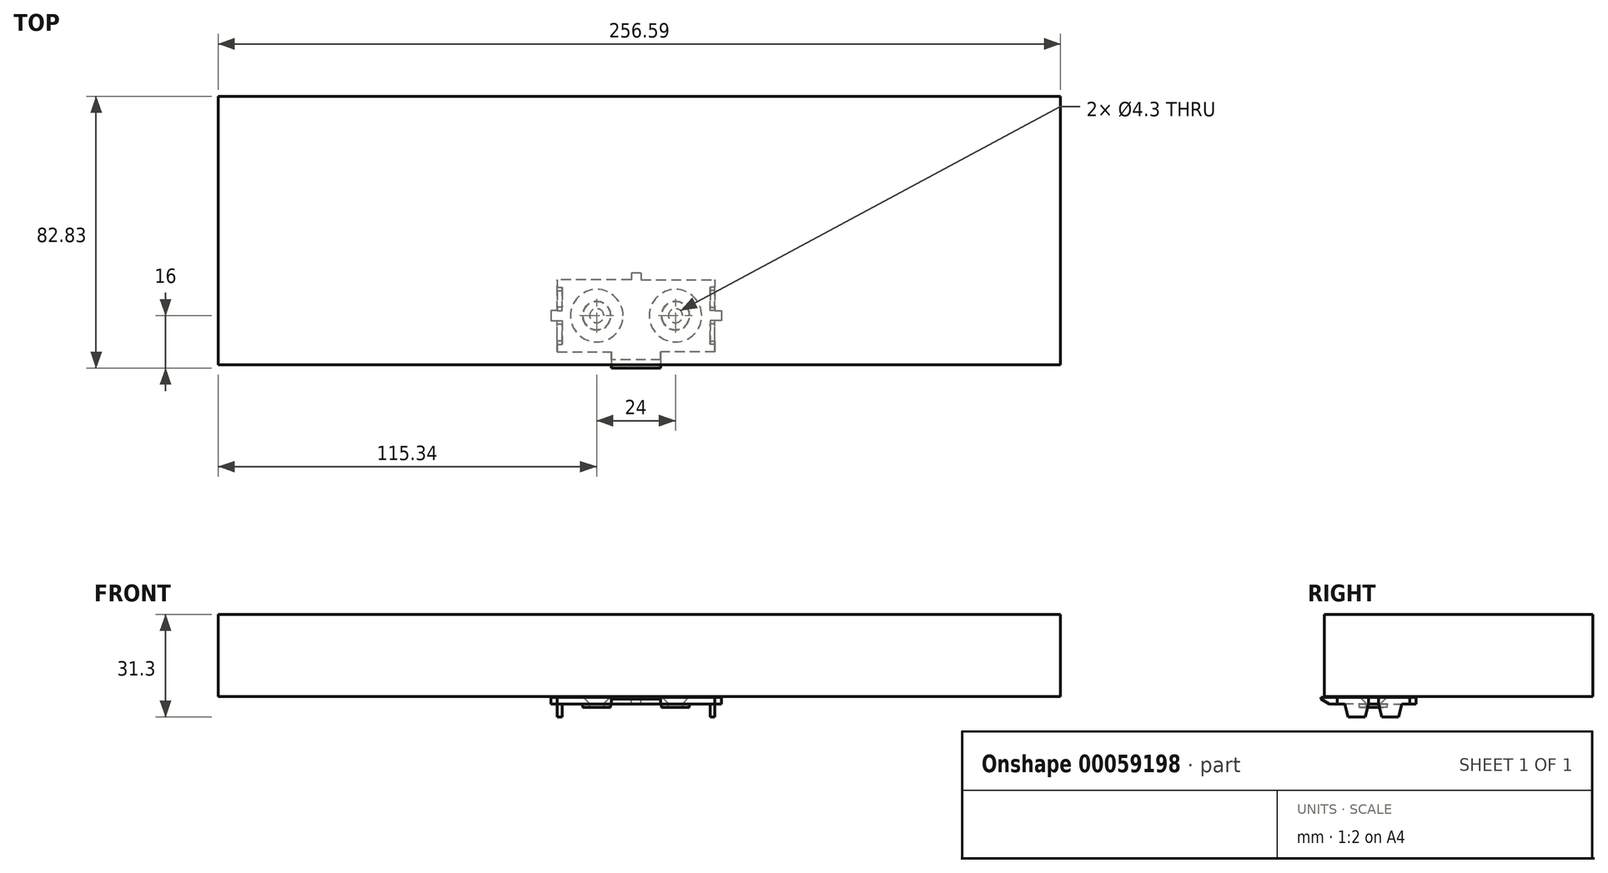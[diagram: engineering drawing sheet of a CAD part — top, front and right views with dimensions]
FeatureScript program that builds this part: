
annotation { "Feature Type Name" : "Feature", "Feature Type Description" : "" }
export const myFeature = defineFeature(function(context is Context, id is Id, definition is map)
    precondition{}
    {
        {
            assignVariable(context, id + "F0", {"name" : "lidLength", "anyValue" : 48 * mm});
        }
        {
            assignVariable(context, id + "F1", {"name" : "lidWidth", "anyValue" : 22 * mm});
        }
        {
            assignVariable(context, id + "F2", {"name" : "lidThickness", "anyValue" : 2 * mm});
        }
        {
            assignVariable(context, id + "F3", {"name" : "lidSnapDistFromTop", "anyValue" : 6 * mm});
        }
        {
            var Q0;
            Q0=qCreatedBy(makeId("Top.planeOp"),FACE);
            cPlane(context, id + "F4", {"entities" : qUnion([Q0]), "cplaneType" : CPlaneType.OFFSET, "offset" : 0.3 * mm, "width" : 150 * mm, "height" : 150 * mm});
        }
        {
            var Q0;
            Q0=qCreatedBy(makeId("Top.planeOp"),FACE);
            cPlane(context, id + "F5", {"entities" : qUnion([Q0]), "cplaneType" : CPlaneType.OFFSET, "offset" : getVariable(context, 'lidThickness'), "oppositeDirection" : true, "width" : 150 * mm, "height" : 150 * mm});
        }
        {
            var Q0;
            Q0=qCreatedBy(makeId("Top.planeOp"),FACE);
            cPlane(context, id + "F6", {"entities" : qUnion([Q0]), "cplaneType" : CPlaneType.OFFSET, "offset" : getVariable(context, 'lidSnapDistFromTop'), "oppositeDirection" : true, "width" : 150 * mm, "height" : 150 * mm});
        }
        {
            var Q0;
            Q0=qCreatedBy(makeId("Top.planeOp"),FACE);
            cPlane(context, id + "F7", {"entities" : qUnion([Q0]), "cplaneType" : CPlaneType.OFFSET, "offset" : 3 * mm, "oppositeDirection" : true, "width" : 150 * mm, "height" : 150 * mm});
        }
        {
            var Q0;
            Q0=qCreatedBy(makeId("Right.planeOp"),FACE);
            cPlane(context, id + "F8", {"entities" : qUnion([Q0]), "cplaneType" : CPlaneType.OFFSET, "offset" : getVariable(context, 'lidLength') / 2, "oppositeDirection" : true, "width" : 150 * mm, "height" : 150 * mm});
        }
        {
            var Q0;
            Q0=qCreatedBy(makeId("Front.planeOp"),FACE);
            cPlane(context, id + "F9", {"entities" : qUnion([Q0]), "cplaneType" : CPlaneType.OFFSET, "offset" : getVariable(context, 'lidWidth'), "oppositeDirection" : true, "width" : 150 * mm, "height" : 150 * mm});
        }
        {
            var Q0;
            Q0=qCreatedBy(makeId("Top.planeOp"),FACE);
            var sketch = newSketch(context, id + "F10", { "sketchPlane" : qUnion([Q0])});
            skLineSegment(sketch, "E0", {"start": v(-7.5, 0) * mm, "end": v(-24, 0) * mm});
            skLineSegment(sketch, "E1", {"start": v(-24, 0) * mm, "end": v(-24, 9.5) * mm});
            skLineSegment(sketch, "E2", {"start": v(-24, 9.5) * mm, "end": v(-26, 9.5) * mm});
            skLineSegment(sketch, "E3", {"start": v(-26, 9.5) * mm, "end": v(-26, 12.5) * mm});
            skLineSegment(sketch, "E4", {"start": v(-26, 12.5) * mm, "end": v(-24, 12.5) * mm});
            skLineSegment(sketch, "E5", {"start": v(-24, 12.5) * mm, "end": v(-24, 22) * mm});
            skLineSegment(sketch, "E6", {"start": v(-24, 22) * mm, "end": v(-1.5, 22) * mm});
            skLineSegment(sketch, "E7", {"start": v(-1.5, 22) * mm, "end": v(-1.5, 24) * mm});
            skLineSegment(sketch, "E8", {"start": v(-1.5, 24) * mm, "end": v(0, 24) * mm});
            skLineSegment(sketch, "E9", {"start": v(-7.5, 0) * mm, "end": v(-7.5, -5) * mm});
            skLineSegment(sketch, "E10", {"start": v(-7.5, -5) * mm, "end": v(0, -5) * mm});
            skLineSegment(sketch, "E11.MirrorCS", {"start": v(24, 9.5) * mm, "end": v(26, 9.5) * mm, "construction": true});
            skLineSegment(sketch, "E12.MirrorCS", {"start": v(7.5, 0) * mm, "end": v(7.5, -5) * mm, "construction": true});
            skLineSegment(sketch, "E13.MirrorCS", {"start": v(26, 12.5) * mm, "end": v(24, 12.5) * mm, "construction": true});
            skLineSegment(sketch, "E14.MirrorCS", {"start": v(1.5, 24) * mm, "end": v(0, 24) * mm, "construction": true});
            skLineSegment(sketch, "E15.MirrorCS", {"start": v(26, 9.5) * mm, "end": v(26, 12.5) * mm, "construction": true});
            skLineSegment(sketch, "E16.MirrorCS", {"start": v(1.5, 22) * mm, "end": v(1.5, 24) * mm, "construction": true});
            skLineSegment(sketch, "E17.MirrorCS", {"start": v(7.5, 0) * mm, "end": v(24, 0) * mm, "construction": true});
            skLineSegment(sketch, "E18.MirrorCS", {"start": v(24, 0) * mm, "end": v(24, 9.5) * mm, "construction": true});
            skLineSegment(sketch, "E19.MirrorCS", {"start": v(7.5, -5) * mm, "end": v(0, -5) * mm, "construction": true});
            skLineSegment(sketch, "E20.MirrorCS", {"start": v(24, 22) * mm, "end": v(1.5, 22) * mm, "construction": true});
            skLineSegment(sketch, "E21.MirrorCS", {"start": v(24, 12.5) * mm, "end": v(24, 22) * mm, "construction": true});
            skLineSegment(sketch, "E22", {"start": v(0, 24) * mm, "end": v(0, -5) * mm});
            skSolve(sketch);
        }
        {
            var Q0;
            Q0 = qSketchRegion(id + "F10", true);
            var Q1;
            Q1=qCreatedBy(id+"F5.planeOp",FACE);
            extrude(context, id + "F11", {"entities" : qUnion([Q0]), "endBound" : BoundingType.UP_TO_SURFACE, "oppositeDirection" : true, "endBoundEntityFace" : qUnion([Q1]), "depth" : 25 * mm});
        }
        {
            var Q0;
            Q0=qCreatedBy(makeId("Top.planeOp"),FACE);
            var sketch = newSketch(context, id + "F12", { "sketchPlane" : qUnion([Q0])});
            skLineSegment(sketch, "E23.bottom", {"start": v(-24, 9.5) * mm, "end": v(-22.5, 9.5) * mm});
            skLineSegment(sketch, "E23.top", {"start": v(-24, 2.3) * mm, "end": v(-22.5, 2.3) * mm});
            skLineSegment(sketch, "E23.left", {"start": v(-24, 9.5) * mm, "end": v(-24, 2.3) * mm});
            skLineSegment(sketch, "E23.right", {"start": v(-22.5, 9.5) * mm, "end": v(-22.5, 2.3) * mm});
            skLineSegment(sketch, "E24.bottom", {"start": v(-24, 12.5) * mm, "end": v(-22.5, 12.5) * mm});
            skLineSegment(sketch, "E24.top", {"start": v(-24, 19.7) * mm, "end": v(-22.5, 19.7) * mm});
            skLineSegment(sketch, "E24.left", {"start": v(-24, 12.5) * mm, "end": v(-24, 19.7) * mm});
            skLineSegment(sketch, "E24.right", {"start": v(-22.5, 12.5) * mm, "end": v(-22.5, 19.7) * mm});
            skSolve(sketch);
        }
        {
            var Q0;
            Q0 = qSketchRegion(id + "F12", true);
            var Q1;
            Q1=qCreatedBy(id+"F6.planeOp",FACE);
            extrude(context, id + "F13", {"entities" : qUnion([Q0]), "operationType" : NewBodyOperationType.ADD, "endBound" : BoundingType.UP_TO_SURFACE, "oppositeDirection" : true, "endBoundEntityFace" : qUnion([Q1]), "depth" : 25 * mm});
        }
        {
            var Q0;
            Q0=qCreatedBy(makeId("Top.planeOp"),FACE);
            var sketch = newSketch(context, id + "F14", { "sketchPlane" : qUnion([Q0])});
            skCircle(sketch, "E25", {"center": v(-12, 11) * mm, "radius": 4.25 * mm});
            skSolve(sketch);
        }
        {
            var Q0;
            Q0 = qSketchRegion(id + "F14", true);
            var Q1;
            Q1=qCreatedBy(id+"F7.planeOp",FACE);
            extrude(context, id + "F15", {"entities" : qUnion([Q0]), "operationType" : NewBodyOperationType.ADD, "endBound" : BoundingType.UP_TO_SURFACE, "oppositeDirection" : true, "endBoundEntityFace" : qUnion([Q1]), "depth" : 25 * mm});
        }
        {
            var Q0;
            Q0=qCreatedBy(makeId("Top.planeOp"),FACE);
            var sketch = newSketch(context, id + "F16", { "sketchPlane" : qUnion([Q0])});
            skCircle(sketch, "E26", {"center": v(-12, 11) * mm, "radius": 8 * mm});
            skSolve(sketch);
        }
        {
            var Q0;
            Q0 = qSketchRegion(id + "F16", true);
            var Q1;
            Q1=qCreatedBy(id+"F4.planeOp",FACE);
            extrude(context, id + "F17", {"entities" : qUnion([Q0]), "operationType" : NewBodyOperationType.ADD, "endBound" : BoundingType.UP_TO_SURFACE, "endBoundEntityFace" : qUnion([Q1]), "depth" : 25 * mm});
        }
        {
            var Q0;
            Q0=qCreatedBy(id+"F4.planeOp",FACE);
            var sketch = newSketch(context, id + "F18", { "sketchPlane" : qUnion([Q0])});
            skPoint(sketch, "E27", {"position": v(-12, 11) * mm});
            skSolve(sketch);
        }
        {
            var Q0;
            Q0=sQuery(id+"F18.wireOp",VERTEX,"E27");
            var Q1;
            Q1=makeQuery(id+"F11.opExtrude","SWEPT_BODY",BODY,{"disambiguationData":[OSD([sQuery(id+"F10.wireOp",EDGE,"E0"),sQuery(id+"F10.wireOp",EDGE,"E1"),sQuery(id+"F10.wireOp",EDGE,"E2"),sQuery(id+"F10.wireOp",EDGE,"E3"),sQuery(id+"F10.wireOp",EDGE,"E4"),sQuery(id+"F10.wireOp",EDGE,"E5"),sQuery(id+"F10.wireOp",EDGE,"E6"),sQuery(id+"F10.wireOp",EDGE,"E7"),sQuery(id+"F10.wireOp",EDGE,"E8"),sQuery(id+"F10.wireOp",EDGE,"E9"),sQuery(id+"F10.wireOp",EDGE,"E10"),sQuery(id+"F10.wireOp",EDGE,"E22")])]});
            hole(context, id + "F19", {"style" : HoleStyle.C_SINK, "holeDiameter" : 4.3 * mm, "cSinkDiameter" : 8.7 * mm, "endStyle" : HoleEndStyle.THROUGH, "locations" : qUnion([Q0]), "scope" : qUnion([Q1]), "cSinkAngle" : 90 * degree});
        }
        {
            var Q0;
            Q0=makeQuery(id+"F11.opExtrude","CAP_EDGE",EDGE,{"disambiguationData":[OSD([sQuery(id+"F10.wireOp",EDGE,"E10")])],"isStart":false});
            chamfer(context, id + "F20", {"entities" : qUnion([Q0]), "chamferType" : ChamferType.TWO_OFFSETS, "width1" : 1.5 * mm, "oppositeDirection" : true, "width2" : 2.5 * mm, "tangentPropagation" : true});
        }
        {
            var Q0;
            Q0=makeQuery(id+"F13.opExtrude","CAP_EDGE",EDGE,{"disambiguationData":[OSD([sQuery(id+"F12.wireOp",EDGE,"E23.top")])],"isStart":false});
            var Q1;
            Q1=makeQuery(id+"F13.opExtrude","CAP_EDGE",EDGE,{"disambiguationData":[OSD([sQuery(id+"F12.wireOp",EDGE,"E24.bottom")])],"isStart":false});
            var Q2;
            Q2=makeQuery(id+"F13.opExtrude","CAP_EDGE",EDGE,{"disambiguationData":[OSD([sQuery(id+"F12.wireOp",EDGE,"E23.bottom")])],"isStart":false});
            chamfer(context, id + "F21", {"entities" : qUnion([Q0, Q1, Q2]), "chamferType" : ChamferType.TWO_OFFSETS, "width1" : getVariable(context, 'lidSnapDistFromTop') - getVariable(context, 'lidThickness'), "oppositeDirection" : true, "width2" : 1 * mm, "tangentPropagation" : true});
        }
        {
            var Q0;
            Q0=makeQuery(id+"F13.opExtrude","CAP_EDGE",EDGE,{"disambiguationData":[OSD([sQuery(id+"F12.wireOp",EDGE,"E24.top")])],"isStart":false});
            chamfer(context, id + "F22", {"entities" : qUnion([Q0]), "chamferType" : ChamferType.TWO_OFFSETS, "width1" : 1 * mm, "oppositeDirection" : true, "width2" : getVariable(context, 'lidSnapDistFromTop') - getVariable(context, 'lidThickness'), "tangentPropagation" : true});
        }
        {
            var Q0;
            Q0=makeQuery(id+"F11.opExtrude","SWEPT_BODY",BODY,{"disambiguationData":[OSD([sQuery(id+"F10.wireOp",EDGE,"E0"),sQuery(id+"F10.wireOp",EDGE,"E1"),sQuery(id+"F10.wireOp",EDGE,"E2"),sQuery(id+"F10.wireOp",EDGE,"E3"),sQuery(id+"F10.wireOp",EDGE,"E4"),sQuery(id+"F10.wireOp",EDGE,"E5"),sQuery(id+"F10.wireOp",EDGE,"E6"),sQuery(id+"F10.wireOp",EDGE,"E7"),sQuery(id+"F10.wireOp",EDGE,"E8"),sQuery(id+"F10.wireOp",EDGE,"E9"),sQuery(id+"F10.wireOp",EDGE,"E10"),sQuery(id+"F10.wireOp",EDGE,"E22")])]});
            var Q1;
            Q1=qCreatedBy(makeId("Right.planeOp"),FACE);
            mirror(context, id + "F23", {"operationType" : NewBodyOperationType.ADD, "entities" : qUnion([Q0]), "mirrorPlane" : qUnion([Q1])});
        }
        {
            var Q0;
            Q0=qCreatedBy(id+"F4.planeOp",FACE);
            var sketch = newSketch(context, id + "F24", { "sketchPlane" : qUnion([Q0])});
            skLineSegment(sketch, "E28.bottom", {"start": v(-127.34, -3.96) * mm, "end": v(129.25, -3.96) * mm});
            skLineSegment(sketch, "E28.top", {"start": v(-127.34, 77.83) * mm, "end": v(129.25, 77.83) * mm});
            skLineSegment(sketch, "E28.left", {"start": v(-127.34, -3.96) * mm, "end": v(-127.34, 77.83) * mm});
            skLineSegment(sketch, "E28.right", {"start": v(129.25, -3.96) * mm, "end": v(129.25, 77.83) * mm});
            skSolve(sketch);
        }
        {
            var Q0;
            Q0 = qSketchRegion(id + "F24", true);
            extrude(context, id + "F25", {"entities" : qUnion([Q0]), "depth" : 25 * mm});
        }
    });
